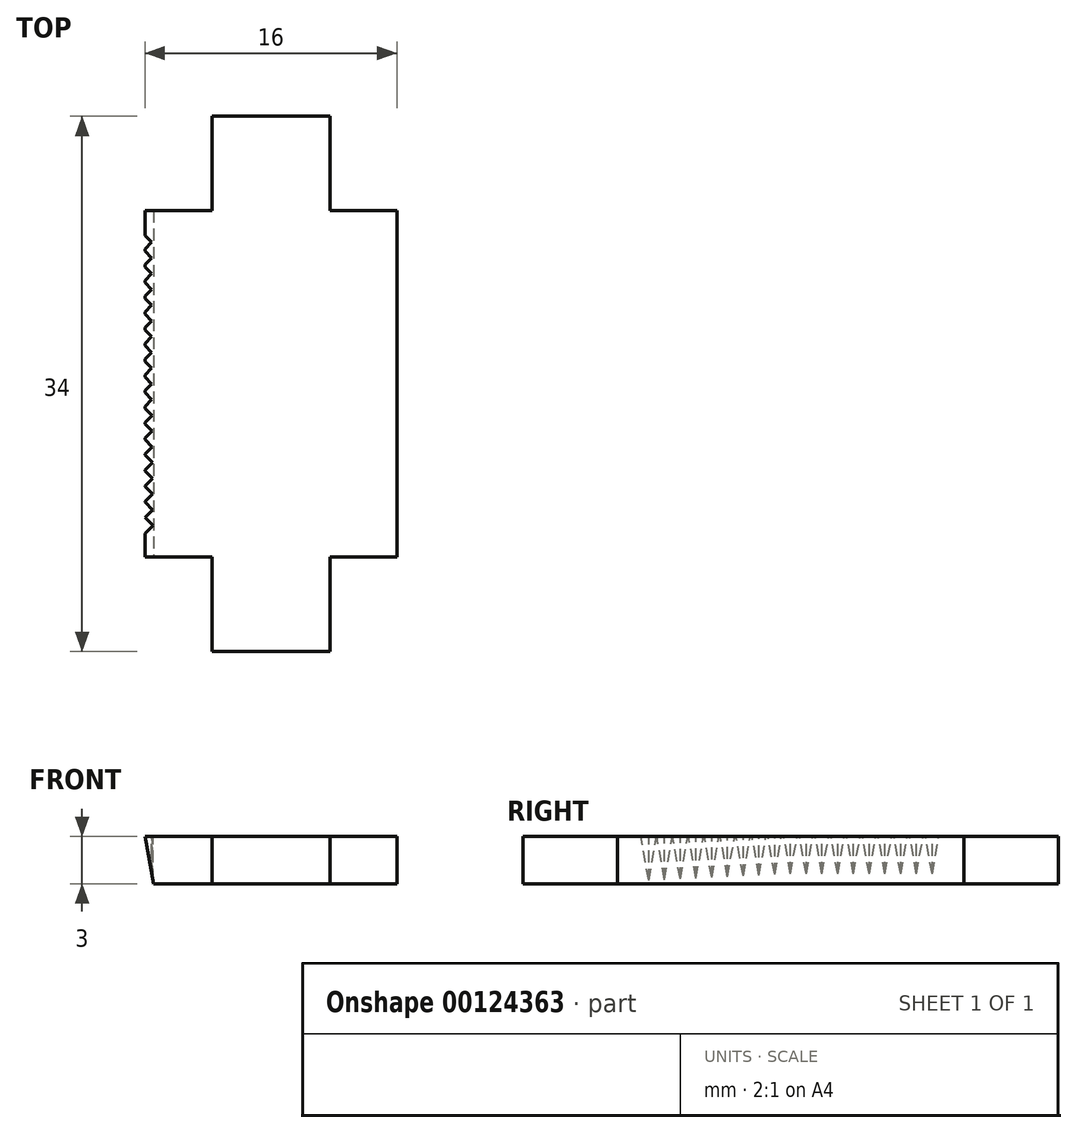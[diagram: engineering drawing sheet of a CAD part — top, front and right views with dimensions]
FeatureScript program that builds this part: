
annotation { "Feature Type Name" : "Feature", "Feature Type Description" : "" }
export const myFeature = defineFeature(function(context is Context, id is Id, definition is map)
    precondition{}
    {
        {
            var Q0;
            Q0=qCreatedBy(makeId("Front.planeOp"),FACE);
            var sketch = newSketch(context, id + "F0", { "sketchPlane" : qUnion([Q0])});
            skLineSegment(sketch, "E0.bottom", {"start": v(8, -1.5) * mm, "end": v(-8, -1.5) * mm});
            skLineSegment(sketch, "E0.top", {"start": v(8, 1.5) * mm, "end": v(-8, 1.5) * mm});
            skLineSegment(sketch, "E0.left", {"start": v(8, -1.5) * mm, "end": v(8, 1.5) * mm});
            skLineSegment(sketch, "E0.right", {"start": v(-8, -1.5) * mm, "end": v(-8, 1.5) * mm});
            skPoint(sketch, "E0.middle", {"position": v(0, 0) * mm});
            skSolve(sketch);
        }
        {
            var Q0;
            Q0=makeQuery(id+"F0.imprint","IMPRINT",FACE,{"disambiguationData":[TD([[makeQuery(id+"F0.imprint","IMPRINT",EDGE,{"derivedFrom":sQuery(id+"F0.wireOp",EDGE,"E0.bottom")}),-1.0]])]});
            extrude(context, id + "F1", {"entities" : qUnion([Q0]), "depth" : 22 * mm});
        }
        {
            var Q0;
            Q0=makeQuery(id+"F1.opExtrude","CAP_FACE",FACE,{"disambiguationData":[OSD([sQuery(id+"F0.wireOp",EDGE,"E0.bottom"),sQuery(id+"F0.wireOp",EDGE,"E0.top"),sQuery(id+"F0.wireOp",EDGE,"E0.left"),sQuery(id+"F0.wireOp",EDGE,"E0.right")])],"isStart":false});
            var sketch = newSketch(context, id + "F2", { "sketchPlane" : qUnion([Q0])});
            skLineSegment(sketch, "E1.bottom", {"start": v(3.75, -1.5) * mm, "end": v(-3.75, -1.5) * mm});
            skLineSegment(sketch, "E1.top", {"start": v(3.75, 1.5) * mm, "end": v(-3.75, 1.5) * mm});
            skLineSegment(sketch, "E1.left", {"start": v(3.75, -1.5) * mm, "end": v(3.75, 1.5) * mm});
            skLineSegment(sketch, "E1.right", {"start": v(-3.75, -1.5) * mm, "end": v(-3.75, 1.5) * mm});
            skPoint(sketch, "E1.middle", {"position": v(0, 0) * mm});
            skSolve(sketch);
        }
        {
            var Q0;
            Q0=makeQuery(id+"F2.imprint","IMPRINT",FACE,{"disambiguationData":[TD([[makeQuery(id+"F2.imprint","IMPRINT",EDGE,{"derivedFrom":sQuery(id+"F2.wireOp",EDGE,"E1.bottom")}),-1.0]])]});
            extrude(context, id + "F3", {"entities" : qUnion([Q0]), "operationType" : NewBodyOperationType.ADD, "depth" : 6 * mm});
        }
        {
            var Q0;
            Q0=makeQuery(id+"F1.opExtrude","CAP_FACE",FACE,{"disambiguationData":[OSD([sQuery(id+"F0.wireOp",EDGE,"E0.bottom"),sQuery(id+"F0.wireOp",EDGE,"E0.top"),sQuery(id+"F0.wireOp",EDGE,"E0.left"),sQuery(id+"F0.wireOp",EDGE,"E0.right")])],"isStart":true});
            var sketch = newSketch(context, id + "F4", { "sketchPlane" : qUnion([Q0])});
            skLineSegment(sketch, "E2.bottom", {"start": v(-3.75, -1.5) * mm, "end": v(3.75, -1.5) * mm});
            skLineSegment(sketch, "E2.top", {"start": v(-3.75, 1.5) * mm, "end": v(3.75, 1.5) * mm});
            skLineSegment(sketch, "E2.left", {"start": v(-3.75, -1.5) * mm, "end": v(-3.75, 1.5) * mm});
            skLineSegment(sketch, "E2.right", {"start": v(3.75, -1.5) * mm, "end": v(3.75, 1.5) * mm});
            skPoint(sketch, "E2.middle", {"position": v(0, 0) * mm});
            skSolve(sketch);
        }
        {
            var Q0;
            Q0=makeQuery(id+"F4.imprint","IMPRINT",FACE,{"disambiguationData":[TD([[makeQuery(id+"F4.imprint","IMPRINT",EDGE,{"derivedFrom":sQuery(id+"F4.wireOp",EDGE,"E2.bottom")}),1.0]])]});
            extrude(context, id + "F5", {"entities" : qUnion([Q0]), "operationType" : NewBodyOperationType.ADD, "depth" : 6 * mm});
        }
        {
            var Q0;
            Q0=makeQuery(id+"F5.boolean.opBoolean","MERGE",FACE,{"derivedFrom":[makeQuery(id+"F3.boolean.opBoolean","MERGE",FACE,{"derivedFrom":[makeQuery(id+"F1.opExtrude","SWEPT_FACE",FACE,{"disambiguationData":[OSD([sQuery(id+"F0.wireOp",EDGE,"E0.top")])]}),makeQuery(id+"F3.opExtrude","SWEPT_FACE",FACE,{"disambiguationData":[OSD([sQuery(id+"F2.wireOp",EDGE,"E1.top")])]})]}),makeQuery(id+"F5.opExtrude","SWEPT_FACE",FACE,{"disambiguationData":[OSD([sQuery(id+"F4.wireOp",EDGE,"E2.top")])]})]});
            var sketch = newSketch(context, id + "F6", { "sketchPlane" : qUnion([Q0])});
            skLineSegment(sketch, "E3", {"start": v(-8, -11) * mm, "end": v(8, -11) * mm, "construction": true});
            skLineSegment(sketch, "E4", {"start": v(-7.5, -11) * mm, "end": v(-8, -10.5) * mm});
            skLineSegment(sketch, "E5", {"start": v(-7.5, -11) * mm, "end": v(-8, -11.5) * mm});
            skPoint(sketch, "E6.orphan", {"position": v(-8.5, -10) * mm});
            skPoint(sketch, "E7.0.1.0", {"position": v(-8.5, -11) * mm});
            skLineSegment(sketch, "E7.0.1.1", {"start": v(-7.5, -12) * mm, "end": v(-8, -12.5) * mm});
            skLineSegment(sketch, "E7.0.1.2", {"start": v(-7.5, -12) * mm, "end": v(-8, -11.5) * mm});
            skPoint(sketch, "E7.0.2.0", {"position": v(-8.5, -12) * mm});
            skLineSegment(sketch, "E7.0.2.1", {"start": v(-7.5, -13) * mm, "end": v(-8, -13.5) * mm});
            skLineSegment(sketch, "E7.0.2.2", {"start": v(-7.5, -13) * mm, "end": v(-8, -12.5) * mm});
            skPoint(sketch, "E7.0.3.0", {"position": v(-8.5, -13) * mm});
            skLineSegment(sketch, "E7.0.3.1", {"start": v(-7.5, -14) * mm, "end": v(-8, -14.5) * mm});
            skLineSegment(sketch, "E7.0.3.2", {"start": v(-7.5, -14) * mm, "end": v(-8, -13.5) * mm});
            skPoint(sketch, "E7.0.4.0", {"position": v(-8.5, -14) * mm});
            skLineSegment(sketch, "E7.0.4.1", {"start": v(-7.5, -15) * mm, "end": v(-8, -15.5) * mm});
            skLineSegment(sketch, "E7.0.4.2", {"start": v(-7.5, -15) * mm, "end": v(-8, -14.5) * mm});
            skPoint(sketch, "E7.0.5.0", {"position": v(-8.5, -15) * mm});
            skLineSegment(sketch, "E7.0.5.1", {"start": v(-7.5, -16) * mm, "end": v(-8, -16.5) * mm});
            skLineSegment(sketch, "E7.0.5.2", {"start": v(-7.5, -16) * mm, "end": v(-8, -15.5) * mm});
            skPoint(sketch, "E7.0.6.0", {"position": v(-8.5, -16) * mm});
            skLineSegment(sketch, "E7.0.6.1", {"start": v(-7.5, -17) * mm, "end": v(-8, -17.5) * mm});
            skLineSegment(sketch, "E7.0.6.2", {"start": v(-7.5, -17) * mm, "end": v(-8, -16.5) * mm});
            skPoint(sketch, "E7.0.7.0", {"position": v(-8.5, -17) * mm});
            skLineSegment(sketch, "E7.0.7.1", {"start": v(-7.5, -18) * mm, "end": v(-8, -18.5) * mm});
            skLineSegment(sketch, "E7.0.7.2", {"start": v(-7.5, -18) * mm, "end": v(-8, -17.5) * mm});
            skPoint(sketch, "E7.0.8.0", {"position": v(-8.5, -18) * mm});
            skLineSegment(sketch, "E7.0.8.1", {"start": v(-7.5, -19) * mm, "end": v(-8, -19.5) * mm});
            skLineSegment(sketch, "E7.0.8.2", {"start": v(-7.5, -19) * mm, "end": v(-8, -18.5) * mm});
            skPoint(sketch, "E7.0.9.0", {"position": v(-8.5, -19) * mm});
            skLineSegment(sketch, "E7.0.9.1", {"start": v(-7.5, -20) * mm, "end": v(-8, -20.5) * mm});
            skLineSegment(sketch, "E7.0.9.2", {"start": v(-7.5, -20) * mm, "end": v(-8, -19.5) * mm});
            skPoint(sketch, "E7.1.0.0", {"position": v(-8.5, -9) * mm});
            skLineSegment(sketch, "E7.1.0.1", {"start": v(-7.5, -10) * mm, "end": v(-8, -10.5) * mm});
            skLineSegment(sketch, "E7.1.0.2", {"start": v(-7.5, -10) * mm, "end": v(-8, -9.5) * mm});
            skPoint(sketch, "E7.1.2.0", {"position": v(-8.5, -11) * mm});
            skLineSegment(sketch, "E7.1.2.1", {"start": v(-7.5, -12) * mm, "end": v(-8, -12.5) * mm});
            skLineSegment(sketch, "E7.1.2.2", {"start": v(-7.5, -12) * mm, "end": v(-8, -11.5) * mm});
            skPoint(sketch, "E7.1.3.0", {"position": v(-8.5, -12) * mm});
            skLineSegment(sketch, "E7.1.3.1", {"start": v(-7.5, -13) * mm, "end": v(-8, -13.5) * mm});
            skLineSegment(sketch, "E7.1.3.2", {"start": v(-7.5, -13) * mm, "end": v(-8, -12.5) * mm});
            skPoint(sketch, "E7.1.4.0", {"position": v(-8.5, -13) * mm});
            skLineSegment(sketch, "E7.1.4.1", {"start": v(-7.5, -14) * mm, "end": v(-8, -14.5) * mm});
            skLineSegment(sketch, "E7.1.4.2", {"start": v(-7.5, -14) * mm, "end": v(-8, -13.5) * mm});
            skPoint(sketch, "E7.1.5.0", {"position": v(-8.5, -14) * mm});
            skLineSegment(sketch, "E7.1.5.1", {"start": v(-7.5, -15) * mm, "end": v(-8, -15.5) * mm});
            skLineSegment(sketch, "E7.1.5.2", {"start": v(-7.5, -15) * mm, "end": v(-8, -14.5) * mm});
            skPoint(sketch, "E7.1.6.0", {"position": v(-8.5, -15) * mm});
            skLineSegment(sketch, "E7.1.6.1", {"start": v(-7.5, -16) * mm, "end": v(-8, -16.5) * mm});
            skLineSegment(sketch, "E7.1.6.2", {"start": v(-7.5, -16) * mm, "end": v(-8, -15.5) * mm});
            skPoint(sketch, "E7.1.7.0", {"position": v(-8.5, -16) * mm});
            skLineSegment(sketch, "E7.1.7.1", {"start": v(-7.5, -17) * mm, "end": v(-8, -17.5) * mm});
            skLineSegment(sketch, "E7.1.7.2", {"start": v(-7.5, -17) * mm, "end": v(-8, -16.5) * mm});
            skPoint(sketch, "E7.1.8.0", {"position": v(-8.5, -17) * mm});
            skLineSegment(sketch, "E7.1.8.1", {"start": v(-7.5, -18) * mm, "end": v(-8, -18.5) * mm});
            skLineSegment(sketch, "E7.1.8.2", {"start": v(-7.5, -18) * mm, "end": v(-8, -17.5) * mm});
            skPoint(sketch, "E7.1.9.0", {"position": v(-8.5, -18) * mm});
            skLineSegment(sketch, "E7.1.9.1", {"start": v(-7.5, -19) * mm, "end": v(-8, -19.5) * mm});
            skLineSegment(sketch, "E7.1.9.2", {"start": v(-7.5, -19) * mm, "end": v(-8, -18.5) * mm});
            skPoint(sketch, "E7.2.0.0", {"position": v(-8.52, -8) * mm});
            skLineSegment(sketch, "E7.2.0.1", {"start": v(-7.52, -9) * mm, "end": v(-8.02, -9.5) * mm});
            skLineSegment(sketch, "E7.2.0.2", {"start": v(-7.52, -9) * mm, "end": v(-8.02, -8.5) * mm});
            skPoint(sketch, "E7.2.1.0", {"position": v(-8.52, -9) * mm});
            skLineSegment(sketch, "E7.2.1.1", {"start": v(-7.52, -10) * mm, "end": v(-8.02, -10.5) * mm});
            skLineSegment(sketch, "E7.2.1.2", {"start": v(-7.52, -10) * mm, "end": v(-8.02, -9.5) * mm});
            skPoint(sketch, "E7.2.2.0", {"position": v(-8.52, -10) * mm});
            skLineSegment(sketch, "E7.2.2.1", {"start": v(-7.52, -11) * mm, "end": v(-8.02, -11.5) * mm});
            skLineSegment(sketch, "E7.2.2.2", {"start": v(-7.52, -11) * mm, "end": v(-8.02, -10.5) * mm});
            skPoint(sketch, "E7.2.3.0", {"position": v(-8.52, -11) * mm});
            skLineSegment(sketch, "E7.2.3.1", {"start": v(-7.52, -12) * mm, "end": v(-8.02, -12.5) * mm});
            skLineSegment(sketch, "E7.2.3.2", {"start": v(-7.52, -12) * mm, "end": v(-8.02, -11.5) * mm});
            skPoint(sketch, "E7.2.4.0", {"position": v(-8.52, -12) * mm});
            skLineSegment(sketch, "E7.2.4.1", {"start": v(-7.52, -13) * mm, "end": v(-8.02, -13.5) * mm});
            skLineSegment(sketch, "E7.2.4.2", {"start": v(-7.52, -13) * mm, "end": v(-8.02, -12.5) * mm});
            skPoint(sketch, "E7.2.5.0", {"position": v(-8.52, -13) * mm});
            skLineSegment(sketch, "E7.2.5.1", {"start": v(-7.52, -14) * mm, "end": v(-8.02, -14.5) * mm});
            skLineSegment(sketch, "E7.2.5.2", {"start": v(-7.52, -14) * mm, "end": v(-8.02, -13.5) * mm});
            skPoint(sketch, "E7.2.6.0", {"position": v(-8.52, -14) * mm});
            skLineSegment(sketch, "E7.2.6.1", {"start": v(-7.52, -15) * mm, "end": v(-8.02, -15.5) * mm});
            skLineSegment(sketch, "E7.2.6.2", {"start": v(-7.52, -15) * mm, "end": v(-8.02, -14.5) * mm});
            skPoint(sketch, "E7.2.7.0", {"position": v(-8.52, -15) * mm});
            skLineSegment(sketch, "E7.2.7.1", {"start": v(-7.52, -16) * mm, "end": v(-8.02, -16.5) * mm});
            skLineSegment(sketch, "E7.2.7.2", {"start": v(-7.52, -16) * mm, "end": v(-8.02, -15.5) * mm});
            skPoint(sketch, "E7.2.8.0", {"position": v(-8.52, -16) * mm});
            skLineSegment(sketch, "E7.2.8.1", {"start": v(-7.52, -17) * mm, "end": v(-8.02, -17.5) * mm});
            skLineSegment(sketch, "E7.2.8.2", {"start": v(-7.52, -17) * mm, "end": v(-8.02, -16.5) * mm});
            skPoint(sketch, "E7.2.9.0", {"position": v(-8.52, -17) * mm});
            skLineSegment(sketch, "E7.2.9.1", {"start": v(-7.52, -18) * mm, "end": v(-8.02, -18.5) * mm});
            skLineSegment(sketch, "E7.2.9.2", {"start": v(-7.52, -18) * mm, "end": v(-8.02, -17.5) * mm});
            skPoint(sketch, "E7.3.0.0", {"position": v(-8.52, -7) * mm});
            skLineSegment(sketch, "E7.3.0.1", {"start": v(-7.52, -8) * mm, "end": v(-8.02, -8.5) * mm});
            skLineSegment(sketch, "E7.3.0.2", {"start": v(-7.52, -8) * mm, "end": v(-8.02, -7.5) * mm});
            skPoint(sketch, "E7.3.1.0", {"position": v(-8.52, -8) * mm});
            skLineSegment(sketch, "E7.3.1.1", {"start": v(-7.52, -9) * mm, "end": v(-8.02, -9.5) * mm});
            skLineSegment(sketch, "E7.3.1.2", {"start": v(-7.52, -9) * mm, "end": v(-8.02, -8.5) * mm});
            skPoint(sketch, "E7.3.2.0", {"position": v(-8.52, -9) * mm});
            skLineSegment(sketch, "E7.3.2.1", {"start": v(-7.52, -10) * mm, "end": v(-8.02, -10.5) * mm});
            skLineSegment(sketch, "E7.3.2.2", {"start": v(-7.52, -10) * mm, "end": v(-8.02, -9.5) * mm});
            skPoint(sketch, "E7.3.3.0", {"position": v(-8.52, -10) * mm});
            skLineSegment(sketch, "E7.3.3.1", {"start": v(-7.52, -11) * mm, "end": v(-8.02, -11.5) * mm});
            skLineSegment(sketch, "E7.3.3.2", {"start": v(-7.52, -11) * mm, "end": v(-8.02, -10.5) * mm});
            skPoint(sketch, "E7.3.4.0", {"position": v(-8.52, -11) * mm});
            skLineSegment(sketch, "E7.3.4.1", {"start": v(-7.52, -12) * mm, "end": v(-8.02, -12.5) * mm});
            skLineSegment(sketch, "E7.3.4.2", {"start": v(-7.52, -12) * mm, "end": v(-8.02, -11.5) * mm});
            skPoint(sketch, "E7.3.5.0", {"position": v(-8.52, -12) * mm});
            skLineSegment(sketch, "E7.3.5.1", {"start": v(-7.52, -13) * mm, "end": v(-8.02, -13.5) * mm});
            skLineSegment(sketch, "E7.3.5.2", {"start": v(-7.52, -13) * mm, "end": v(-8.02, -12.5) * mm});
            skPoint(sketch, "E7.3.6.0", {"position": v(-8.52, -13) * mm});
            skLineSegment(sketch, "E7.3.6.1", {"start": v(-7.52, -14) * mm, "end": v(-8.02, -14.5) * mm});
            skLineSegment(sketch, "E7.3.6.2", {"start": v(-7.52, -14) * mm, "end": v(-8.02, -13.5) * mm});
            skPoint(sketch, "E7.3.7.0", {"position": v(-8.52, -14) * mm});
            skLineSegment(sketch, "E7.3.7.1", {"start": v(-7.52, -15) * mm, "end": v(-8.02, -15.5) * mm});
            skLineSegment(sketch, "E7.3.7.2", {"start": v(-7.52, -15) * mm, "end": v(-8.02, -14.5) * mm});
            skPoint(sketch, "E7.3.8.0", {"position": v(-8.52, -15) * mm});
            skLineSegment(sketch, "E7.3.8.1", {"start": v(-7.52, -16) * mm, "end": v(-8.02, -16.5) * mm});
            skLineSegment(sketch, "E7.3.8.2", {"start": v(-7.52, -16) * mm, "end": v(-8.02, -15.5) * mm});
            skPoint(sketch, "E7.3.9.0", {"position": v(-8.52, -16) * mm});
            skLineSegment(sketch, "E7.3.9.1", {"start": v(-7.52, -17) * mm, "end": v(-8.02, -17.5) * mm});
            skLineSegment(sketch, "E7.3.9.2", {"start": v(-7.52, -17) * mm, "end": v(-8.02, -16.5) * mm});
            skPoint(sketch, "E7.4.0.0", {"position": v(-8.53, -6) * mm});
            skLineSegment(sketch, "E7.4.0.1", {"start": v(-7.53, -7) * mm, "end": v(-8.03, -7.5) * mm});
            skLineSegment(sketch, "E7.4.0.2", {"start": v(-7.53, -7) * mm, "end": v(-8.03, -6.5) * mm});
            skPoint(sketch, "E7.4.1.0", {"position": v(-8.53, -7) * mm});
            skLineSegment(sketch, "E7.4.1.1", {"start": v(-7.53, -8) * mm, "end": v(-8.03, -8.5) * mm});
            skLineSegment(sketch, "E7.4.1.2", {"start": v(-7.53, -8) * mm, "end": v(-8.03, -7.5) * mm});
            skPoint(sketch, "E7.4.2.0", {"position": v(-8.53, -8) * mm});
            skLineSegment(sketch, "E7.4.2.1", {"start": v(-7.53, -9) * mm, "end": v(-8.03, -9.5) * mm});
            skLineSegment(sketch, "E7.4.2.2", {"start": v(-7.53, -9) * mm, "end": v(-8.03, -8.5) * mm});
            skPoint(sketch, "E7.4.3.0", {"position": v(-8.53, -9) * mm});
            skLineSegment(sketch, "E7.4.3.1", {"start": v(-7.53, -10) * mm, "end": v(-8.03, -10.5) * mm});
            skLineSegment(sketch, "E7.4.3.2", {"start": v(-7.53, -10) * mm, "end": v(-8.03, -9.5) * mm});
            skPoint(sketch, "E7.4.4.0", {"position": v(-8.53, -10) * mm});
            skLineSegment(sketch, "E7.4.4.1", {"start": v(-7.53, -11) * mm, "end": v(-8.03, -11.5) * mm});
            skLineSegment(sketch, "E7.4.4.2", {"start": v(-7.53, -11) * mm, "end": v(-8.03, -10.5) * mm});
            skPoint(sketch, "E7.4.5.0", {"position": v(-8.53, -11) * mm});
            skLineSegment(sketch, "E7.4.5.1", {"start": v(-7.53, -12) * mm, "end": v(-8.03, -12.5) * mm});
            skLineSegment(sketch, "E7.4.5.2", {"start": v(-7.53, -12) * mm, "end": v(-8.03, -11.5) * mm});
            skPoint(sketch, "E7.4.6.0", {"position": v(-8.53, -12) * mm});
            skLineSegment(sketch, "E7.4.6.1", {"start": v(-7.53, -13) * mm, "end": v(-8.03, -13.5) * mm});
            skLineSegment(sketch, "E7.4.6.2", {"start": v(-7.53, -13) * mm, "end": v(-8.03, -12.5) * mm});
            skPoint(sketch, "E7.4.7.0", {"position": v(-8.53, -13) * mm});
            skLineSegment(sketch, "E7.4.7.1", {"start": v(-7.53, -14) * mm, "end": v(-8.03, -14.5) * mm});
            skLineSegment(sketch, "E7.4.7.2", {"start": v(-7.53, -14) * mm, "end": v(-8.03, -13.5) * mm});
            skPoint(sketch, "E7.4.8.0", {"position": v(-8.53, -14) * mm});
            skLineSegment(sketch, "E7.4.8.1", {"start": v(-7.53, -15) * mm, "end": v(-8.03, -15.5) * mm});
            skLineSegment(sketch, "E7.4.8.2", {"start": v(-7.53, -15) * mm, "end": v(-8.03, -14.5) * mm});
            skPoint(sketch, "E7.4.9.0", {"position": v(-8.53, -15) * mm});
            skLineSegment(sketch, "E7.4.9.1", {"start": v(-7.53, -16) * mm, "end": v(-8.03, -16.5) * mm});
            skLineSegment(sketch, "E7.4.9.2", {"start": v(-7.53, -16) * mm, "end": v(-8.03, -15.5) * mm});
            skPoint(sketch, "E7.5.0.0", {"position": v(-8.54, -5) * mm});
            skLineSegment(sketch, "E7.5.0.1", {"start": v(-7.54, -6) * mm, "end": v(-8.04, -6.5) * mm});
            skLineSegment(sketch, "E7.5.0.2", {"start": v(-7.54, -6) * mm, "end": v(-8.04, -5.5) * mm});
            skPoint(sketch, "E7.5.1.0", {"position": v(-8.54, -6) * mm});
            skLineSegment(sketch, "E7.5.1.1", {"start": v(-7.54, -7) * mm, "end": v(-8.04, -7.5) * mm});
            skLineSegment(sketch, "E7.5.1.2", {"start": v(-7.54, -7) * mm, "end": v(-8.04, -6.5) * mm});
            skPoint(sketch, "E7.5.2.0", {"position": v(-8.54, -7) * mm});
            skLineSegment(sketch, "E7.5.2.1", {"start": v(-7.54, -8) * mm, "end": v(-8.04, -8.5) * mm});
            skLineSegment(sketch, "E7.5.2.2", {"start": v(-7.54, -8) * mm, "end": v(-8.04, -7.5) * mm});
            skPoint(sketch, "E7.5.3.0", {"position": v(-8.54, -8) * mm});
            skLineSegment(sketch, "E7.5.3.1", {"start": v(-7.54, -9) * mm, "end": v(-8.04, -9.5) * mm});
            skLineSegment(sketch, "E7.5.3.2", {"start": v(-7.54, -9) * mm, "end": v(-8.04, -8.5) * mm});
            skPoint(sketch, "E7.5.4.0", {"position": v(-8.54, -9) * mm});
            skLineSegment(sketch, "E7.5.4.1", {"start": v(-7.54, -10) * mm, "end": v(-8.04, -10.5) * mm});
            skLineSegment(sketch, "E7.5.4.2", {"start": v(-7.54, -10) * mm, "end": v(-8.04, -9.5) * mm});
            skPoint(sketch, "E7.5.5.0", {"position": v(-8.54, -10) * mm});
            skLineSegment(sketch, "E7.5.5.1", {"start": v(-7.54, -11) * mm, "end": v(-8.04, -11.5) * mm});
            skLineSegment(sketch, "E7.5.5.2", {"start": v(-7.54, -11) * mm, "end": v(-8.04, -10.5) * mm});
            skPoint(sketch, "E7.5.6.0", {"position": v(-8.54, -11) * mm});
            skLineSegment(sketch, "E7.5.6.1", {"start": v(-7.54, -12) * mm, "end": v(-8.04, -12.5) * mm});
            skLineSegment(sketch, "E7.5.6.2", {"start": v(-7.54, -12) * mm, "end": v(-8.04, -11.5) * mm});
            skPoint(sketch, "E7.5.7.0", {"position": v(-8.54, -12) * mm});
            skLineSegment(sketch, "E7.5.7.1", {"start": v(-7.54, -13) * mm, "end": v(-8.04, -13.5) * mm});
            skLineSegment(sketch, "E7.5.7.2", {"start": v(-7.54, -13) * mm, "end": v(-8.04, -12.5) * mm});
            skPoint(sketch, "E7.5.8.0", {"position": v(-8.54, -13) * mm});
            skLineSegment(sketch, "E7.5.8.1", {"start": v(-7.54, -14) * mm, "end": v(-8.04, -14.5) * mm});
            skLineSegment(sketch, "E7.5.8.2", {"start": v(-7.54, -14) * mm, "end": v(-8.04, -13.5) * mm});
            skPoint(sketch, "E7.5.9.0", {"position": v(-8.54, -14) * mm});
            skLineSegment(sketch, "E7.5.9.1", {"start": v(-7.54, -15) * mm, "end": v(-8.04, -15.5) * mm});
            skLineSegment(sketch, "E7.5.9.2", {"start": v(-7.54, -15) * mm, "end": v(-8.04, -14.5) * mm});
            skPoint(sketch, "E7.6.0.0", {"position": v(-8.55, -4) * mm});
            skLineSegment(sketch, "E7.6.0.1", {"start": v(-7.55, -5) * mm, "end": v(-8.05, -5.5) * mm});
            skLineSegment(sketch, "E7.6.0.2", {"start": v(-7.55, -5) * mm, "end": v(-8.05, -4.5) * mm});
            skPoint(sketch, "E7.6.1.0", {"position": v(-8.55, -5) * mm});
            skLineSegment(sketch, "E7.6.1.1", {"start": v(-7.55, -6) * mm, "end": v(-8.05, -6.5) * mm});
            skLineSegment(sketch, "E7.6.1.2", {"start": v(-7.55, -6) * mm, "end": v(-8.05, -5.5) * mm});
            skPoint(sketch, "E7.6.2.0", {"position": v(-8.55, -6) * mm});
            skLineSegment(sketch, "E7.6.2.1", {"start": v(-7.55, -7) * mm, "end": v(-8.05, -7.5) * mm});
            skLineSegment(sketch, "E7.6.2.2", {"start": v(-7.55, -7) * mm, "end": v(-8.05, -6.5) * mm});
            skPoint(sketch, "E7.6.3.0", {"position": v(-8.55, -7) * mm});
            skLineSegment(sketch, "E7.6.3.1", {"start": v(-7.55, -8) * mm, "end": v(-8.05, -8.5) * mm});
            skLineSegment(sketch, "E7.6.3.2", {"start": v(-7.55, -8) * mm, "end": v(-8.05, -7.5) * mm});
            skPoint(sketch, "E7.6.4.0", {"position": v(-8.55, -8) * mm});
            skLineSegment(sketch, "E7.6.4.1", {"start": v(-7.55, -9) * mm, "end": v(-8.05, -9.5) * mm});
            skLineSegment(sketch, "E7.6.4.2", {"start": v(-7.55, -9) * mm, "end": v(-8.05, -8.5) * mm});
            skPoint(sketch, "E7.6.5.0", {"position": v(-8.55, -9) * mm});
            skLineSegment(sketch, "E7.6.5.1", {"start": v(-7.55, -10) * mm, "end": v(-8.05, -10.5) * mm});
            skLineSegment(sketch, "E7.6.5.2", {"start": v(-7.55, -10) * mm, "end": v(-8.05, -9.5) * mm});
            skPoint(sketch, "E7.6.6.0", {"position": v(-8.55, -10) * mm});
            skLineSegment(sketch, "E7.6.6.1", {"start": v(-7.55, -11) * mm, "end": v(-8.05, -11.5) * mm});
            skLineSegment(sketch, "E7.6.6.2", {"start": v(-7.55, -11) * mm, "end": v(-8.05, -10.5) * mm});
            skPoint(sketch, "E7.6.7.0", {"position": v(-8.55, -11) * mm});
            skLineSegment(sketch, "E7.6.7.1", {"start": v(-7.55, -12) * mm, "end": v(-8.05, -12.5) * mm});
            skLineSegment(sketch, "E7.6.7.2", {"start": v(-7.55, -12) * mm, "end": v(-8.05, -11.5) * mm});
            skPoint(sketch, "E7.6.8.0", {"position": v(-8.55, -12) * mm});
            skLineSegment(sketch, "E7.6.8.1", {"start": v(-7.55, -13) * mm, "end": v(-8.05, -13.5) * mm});
            skLineSegment(sketch, "E7.6.8.2", {"start": v(-7.55, -13) * mm, "end": v(-8.05, -12.5) * mm});
            skPoint(sketch, "E7.6.9.0", {"position": v(-8.55, -13) * mm});
            skLineSegment(sketch, "E7.6.9.1", {"start": v(-7.55, -14) * mm, "end": v(-8.05, -14.5) * mm});
            skLineSegment(sketch, "E7.6.9.2", {"start": v(-7.55, -14) * mm, "end": v(-8.05, -13.5) * mm});
            skPoint(sketch, "E7.7.0.0", {"position": v(-8.56, -3) * mm});
            skLineSegment(sketch, "E7.7.0.1", {"start": v(-7.56, -4) * mm, "end": v(-8.06, -4.5) * mm});
            skLineSegment(sketch, "E7.7.0.2", {"start": v(-7.56, -4) * mm, "end": v(-8.06, -3.5) * mm});
            skPoint(sketch, "E7.7.1.0", {"position": v(-8.56, -4) * mm});
            skLineSegment(sketch, "E7.7.1.1", {"start": v(-7.56, -5) * mm, "end": v(-8.06, -5.5) * mm});
            skLineSegment(sketch, "E7.7.1.2", {"start": v(-7.56, -5) * mm, "end": v(-8.06, -4.5) * mm});
            skPoint(sketch, "E7.7.2.0", {"position": v(-8.56, -5) * mm});
            skLineSegment(sketch, "E7.7.2.1", {"start": v(-7.56, -6) * mm, "end": v(-8.06, -6.5) * mm});
            skLineSegment(sketch, "E7.7.2.2", {"start": v(-7.56, -6) * mm, "end": v(-8.06, -5.5) * mm});
            skPoint(sketch, "E7.7.3.0", {"position": v(-8.56, -6) * mm});
            skLineSegment(sketch, "E7.7.3.1", {"start": v(-7.56, -7) * mm, "end": v(-8.06, -7.5) * mm});
            skLineSegment(sketch, "E7.7.3.2", {"start": v(-7.56, -7) * mm, "end": v(-8.06, -6.5) * mm});
            skPoint(sketch, "E7.7.4.0", {"position": v(-8.56, -7) * mm});
            skLineSegment(sketch, "E7.7.4.1", {"start": v(-7.56, -8) * mm, "end": v(-8.06, -8.5) * mm});
            skLineSegment(sketch, "E7.7.4.2", {"start": v(-7.56, -8) * mm, "end": v(-8.06, -7.5) * mm});
            skPoint(sketch, "E7.7.5.0", {"position": v(-8.56, -8) * mm});
            skLineSegment(sketch, "E7.7.5.1", {"start": v(-7.56, -9) * mm, "end": v(-8.06, -9.5) * mm});
            skLineSegment(sketch, "E7.7.5.2", {"start": v(-7.56, -9) * mm, "end": v(-8.06, -8.5) * mm});
            skPoint(sketch, "E7.7.6.0", {"position": v(-8.56, -9) * mm});
            skLineSegment(sketch, "E7.7.6.1", {"start": v(-7.56, -10) * mm, "end": v(-8.06, -10.5) * mm});
            skLineSegment(sketch, "E7.7.6.2", {"start": v(-7.56, -10) * mm, "end": v(-8.06, -9.5) * mm});
            skPoint(sketch, "E7.7.7.0", {"position": v(-8.56, -10) * mm});
            skLineSegment(sketch, "E7.7.7.1", {"start": v(-7.56, -11) * mm, "end": v(-8.06, -11.5) * mm});
            skLineSegment(sketch, "E7.7.7.2", {"start": v(-7.56, -11) * mm, "end": v(-8.06, -10.5) * mm});
            skPoint(sketch, "E7.7.8.0", {"position": v(-8.56, -11) * mm});
            skLineSegment(sketch, "E7.7.8.1", {"start": v(-7.56, -12) * mm, "end": v(-8.06, -12.5) * mm});
            skLineSegment(sketch, "E7.7.8.2", {"start": v(-7.56, -12) * mm, "end": v(-8.06, -11.5) * mm});
            skPoint(sketch, "E7.7.9.0", {"position": v(-8.56, -12) * mm});
            skLineSegment(sketch, "E7.7.9.1", {"start": v(-7.56, -13) * mm, "end": v(-8.06, -13.5) * mm});
            skLineSegment(sketch, "E7.7.9.2", {"start": v(-7.56, -13) * mm, "end": v(-8.06, -12.5) * mm});
            skPoint(sketch, "E7.8.0.0", {"position": v(-8.57, -2) * mm});
            skLineSegment(sketch, "E7.8.0.1", {"start": v(-7.57, -3) * mm, "end": v(-8.07, -3.5) * mm});
            skLineSegment(sketch, "E7.8.0.2", {"start": v(-7.57, -3) * mm, "end": v(-8.07, -2.5) * mm});
            skPoint(sketch, "E7.8.1.0", {"position": v(-8.57, -3) * mm});
            skLineSegment(sketch, "E7.8.1.1", {"start": v(-7.57, -4) * mm, "end": v(-8.07, -4.5) * mm});
            skLineSegment(sketch, "E7.8.1.2", {"start": v(-7.57, -4) * mm, "end": v(-8.07, -3.5) * mm});
            skPoint(sketch, "E7.8.2.0", {"position": v(-8.57, -4) * mm});
            skLineSegment(sketch, "E7.8.2.1", {"start": v(-7.57, -5) * mm, "end": v(-8.07, -5.5) * mm});
            skLineSegment(sketch, "E7.8.2.2", {"start": v(-7.57, -5) * mm, "end": v(-8.07, -4.5) * mm});
            skPoint(sketch, "E7.8.3.0", {"position": v(-8.57, -5) * mm});
            skLineSegment(sketch, "E7.8.3.1", {"start": v(-7.57, -6) * mm, "end": v(-8.07, -6.5) * mm});
            skLineSegment(sketch, "E7.8.3.2", {"start": v(-7.57, -6) * mm, "end": v(-8.07, -5.5) * mm});
            skPoint(sketch, "E7.8.4.0", {"position": v(-8.57, -6) * mm});
            skLineSegment(sketch, "E7.8.4.1", {"start": v(-7.57, -7) * mm, "end": v(-8.07, -7.5) * mm});
            skLineSegment(sketch, "E7.8.4.2", {"start": v(-7.57, -7) * mm, "end": v(-8.07, -6.5) * mm});
            skPoint(sketch, "E7.8.5.0", {"position": v(-8.57, -7) * mm});
            skLineSegment(sketch, "E7.8.5.1", {"start": v(-7.57, -8) * mm, "end": v(-8.07, -8.5) * mm});
            skLineSegment(sketch, "E7.8.5.2", {"start": v(-7.57, -8) * mm, "end": v(-8.07, -7.5) * mm});
            skPoint(sketch, "E7.8.6.0", {"position": v(-8.57, -8) * mm});
            skLineSegment(sketch, "E7.8.6.1", {"start": v(-7.57, -9) * mm, "end": v(-8.07, -9.5) * mm});
            skLineSegment(sketch, "E7.8.6.2", {"start": v(-7.57, -9) * mm, "end": v(-8.07, -8.5) * mm});
            skPoint(sketch, "E7.8.7.0", {"position": v(-8.57, -9) * mm});
            skLineSegment(sketch, "E7.8.7.1", {"start": v(-7.57, -10) * mm, "end": v(-8.07, -10.5) * mm});
            skLineSegment(sketch, "E7.8.7.2", {"start": v(-7.57, -10) * mm, "end": v(-8.07, -9.5) * mm});
            skPoint(sketch, "E7.8.8.0", {"position": v(-8.57, -10) * mm});
            skLineSegment(sketch, "E7.8.8.1", {"start": v(-7.57, -11) * mm, "end": v(-8.07, -11.5) * mm});
            skLineSegment(sketch, "E7.8.8.2", {"start": v(-7.57, -11) * mm, "end": v(-8.07, -10.5) * mm});
            skPoint(sketch, "E7.8.9.0", {"position": v(-8.57, -11) * mm});
            skLineSegment(sketch, "E7.8.9.1", {"start": v(-7.57, -12) * mm, "end": v(-8.07, -12.5) * mm});
            skLineSegment(sketch, "E7.8.9.2", {"start": v(-7.57, -12) * mm, "end": v(-8.07, -11.5) * mm});
            skPoint(sketch, "E7.9.0.0", {"position": v(-8.57, -1) * mm});
            skLineSegment(sketch, "E7.9.0.1", {"start": v(-7.57, -2) * mm, "end": v(-8.07, -2.5) * mm});
            skLineSegment(sketch, "E7.9.0.2", {"start": v(-7.57, -2) * mm, "end": v(-8.07, -1.5) * mm});
            skPoint(sketch, "E7.9.1.0", {"position": v(-8.57, -2) * mm});
            skLineSegment(sketch, "E7.9.1.1", {"start": v(-7.57, -3) * mm, "end": v(-8.07, -3.5) * mm});
            skLineSegment(sketch, "E7.9.1.2", {"start": v(-7.57, -3) * mm, "end": v(-8.07, -2.5) * mm});
            skPoint(sketch, "E7.9.2.0", {"position": v(-8.57, -3) * mm});
            skLineSegment(sketch, "E7.9.2.1", {"start": v(-7.57, -4) * mm, "end": v(-8.07, -4.5) * mm});
            skLineSegment(sketch, "E7.9.2.2", {"start": v(-7.57, -4) * mm, "end": v(-8.07, -3.5) * mm});
            skPoint(sketch, "E7.9.3.0", {"position": v(-8.57, -4) * mm});
            skLineSegment(sketch, "E7.9.3.1", {"start": v(-7.57, -5) * mm, "end": v(-8.07, -5.5) * mm});
            skLineSegment(sketch, "E7.9.3.2", {"start": v(-7.57, -5) * mm, "end": v(-8.07, -4.5) * mm});
            skPoint(sketch, "E7.9.4.0", {"position": v(-8.57, -5) * mm});
            skLineSegment(sketch, "E7.9.4.1", {"start": v(-7.57, -6) * mm, "end": v(-8.07, -6.5) * mm});
            skLineSegment(sketch, "E7.9.4.2", {"start": v(-7.57, -6) * mm, "end": v(-8.07, -5.5) * mm});
            skPoint(sketch, "E7.9.5.0", {"position": v(-8.57, -6) * mm});
            skLineSegment(sketch, "E7.9.5.1", {"start": v(-7.57, -7) * mm, "end": v(-8.07, -7.5) * mm});
            skLineSegment(sketch, "E7.9.5.2", {"start": v(-7.57, -7) * mm, "end": v(-8.07, -6.5) * mm});
            skPoint(sketch, "E7.9.6.0", {"position": v(-8.57, -7) * mm});
            skLineSegment(sketch, "E7.9.6.1", {"start": v(-7.57, -8) * mm, "end": v(-8.07, -8.5) * mm});
            skLineSegment(sketch, "E7.9.6.2", {"start": v(-7.57, -8) * mm, "end": v(-8.07, -7.5) * mm});
            skPoint(sketch, "E7.9.7.0", {"position": v(-8.57, -8) * mm});
            skLineSegment(sketch, "E7.9.7.1", {"start": v(-7.57, -9) * mm, "end": v(-8.07, -9.5) * mm});
            skLineSegment(sketch, "E7.9.7.2", {"start": v(-7.57, -9) * mm, "end": v(-8.07, -8.5) * mm});
            skPoint(sketch, "E7.9.8.0", {"position": v(-8.57, -9) * mm});
            skLineSegment(sketch, "E7.9.8.1", {"start": v(-7.57, -10) * mm, "end": v(-8.07, -10.5) * mm});
            skLineSegment(sketch, "E7.9.8.2", {"start": v(-7.57, -10) * mm, "end": v(-8.07, -9.5) * mm});
            skPoint(sketch, "E7.9.9.0", {"position": v(-8.57, -10) * mm});
            skLineSegment(sketch, "E7.9.9.1", {"start": v(-7.57, -11) * mm, "end": v(-8.07, -11.5) * mm});
            skLineSegment(sketch, "E7.9.9.2", {"start": v(-7.57, -11) * mm, "end": v(-8.07, -10.5) * mm});
            skLineSegment(sketch, "E7.direction1", {"start": v(-8, -11.5) * mm, "end": v(-8, -10.5) * mm, "construction": true});
            skLineSegment(sketch, "E7.direction2", {"start": v(-8, -11.5) * mm, "end": v(-8, -12.5) * mm, "construction": true});
            skSolve(sketch);
        }
        {
            var Q0;
            Q0 = qSketchRegion(id + "F6", true);
            var Q1;
            {var subQ0=sQuery(id+"F6.wireOp",EDGE,"E7.9.0.2");var subQ1=sQuery(id+"F6.wireOp",EDGE,"E7.9.0.1");var subQ2=makeQuery(id+"F6.imprint","INTERSECT",VERTEX,{"derivedFrom":[subQ1,subQ0]});Q1=makeQuery(id+"F6.imprint","IMPRINT",FACE,{"disambiguationData":[TD([[makeQuery(id+"F6.imprint","IMPRINT",EDGE,{"disambiguationData":[TD([[subQ2,-1.0]])],"derivedFrom":subQ1}),-1.0]])]});}
            var Q2;
            {var subQ0=sQuery(id+"F6.wireOp",EDGE,"E7.9.1.2");var subQ1=sQuery(id+"F6.wireOp",EDGE,"E7.9.1.1");var subQ2=makeQuery(id+"F6.imprint","INTERSECT",VERTEX,{"derivedFrom":[subQ1,subQ0]});Q2=makeQuery(id+"F6.imprint","IMPRINT",FACE,{"disambiguationData":[TD([[makeQuery(id+"F6.imprint","IMPRINT",EDGE,{"disambiguationData":[TD([[subQ2,-1.0]])],"derivedFrom":subQ1}),-1.0]])]});}
            var Q3;
            {var subQ0=sQuery(id+"F6.wireOp",EDGE,"E7.9.2.2");var subQ1=sQuery(id+"F6.wireOp",EDGE,"E7.9.2.1");var subQ2=makeQuery(id+"F6.imprint","INTERSECT",VERTEX,{"derivedFrom":[subQ1,subQ0]});Q3=makeQuery(id+"F6.imprint","IMPRINT",FACE,{"disambiguationData":[TD([[makeQuery(id+"F6.imprint","IMPRINT",EDGE,{"disambiguationData":[TD([[subQ2,-1.0]])],"derivedFrom":subQ1}),-1.0]])]});}
            var Q4;
            {var subQ0=sQuery(id+"F6.wireOp",EDGE,"E7.9.3.2");var subQ1=sQuery(id+"F6.wireOp",EDGE,"E7.9.3.1");var subQ2=makeQuery(id+"F6.imprint","INTERSECT",VERTEX,{"derivedFrom":[subQ1,subQ0]});Q4=makeQuery(id+"F6.imprint","IMPRINT",FACE,{"disambiguationData":[TD([[makeQuery(id+"F6.imprint","IMPRINT",EDGE,{"disambiguationData":[TD([[subQ2,-1.0]])],"derivedFrom":subQ1}),-1.0]])]});}
            var Q5;
            {var subQ0=sQuery(id+"F6.wireOp",EDGE,"E7.9.4.2");var subQ1=sQuery(id+"F6.wireOp",EDGE,"E7.9.4.1");var subQ2=makeQuery(id+"F6.imprint","INTERSECT",VERTEX,{"derivedFrom":[subQ1,subQ0]});Q5=makeQuery(id+"F6.imprint","IMPRINT",FACE,{"disambiguationData":[TD([[makeQuery(id+"F6.imprint","IMPRINT",EDGE,{"disambiguationData":[TD([[subQ2,-1.0]])],"derivedFrom":subQ1}),-1.0]])]});}
            var Q6;
            {var subQ0=sQuery(id+"F6.wireOp",EDGE,"E7.9.5.2");var subQ1=sQuery(id+"F6.wireOp",EDGE,"E7.9.5.1");var subQ2=makeQuery(id+"F6.imprint","INTERSECT",VERTEX,{"derivedFrom":[subQ1,subQ0]});Q6=makeQuery(id+"F6.imprint","IMPRINT",FACE,{"disambiguationData":[TD([[makeQuery(id+"F6.imprint","IMPRINT",EDGE,{"disambiguationData":[TD([[subQ2,-1.0]])],"derivedFrom":subQ1}),-1.0]])]});}
            var Q7;
            {var subQ0=sQuery(id+"F6.wireOp",EDGE,"E7.9.6.2");var subQ1=sQuery(id+"F6.wireOp",EDGE,"E7.9.6.1");var subQ2=makeQuery(id+"F6.imprint","INTERSECT",VERTEX,{"derivedFrom":[subQ1,subQ0]});Q7=makeQuery(id+"F6.imprint","IMPRINT",FACE,{"disambiguationData":[TD([[makeQuery(id+"F6.imprint","IMPRINT",EDGE,{"disambiguationData":[TD([[subQ2,-1.0]])],"derivedFrom":subQ1}),-1.0]])]});}
            var Q8;
            {var subQ0=sQuery(id+"F6.wireOp",EDGE,"E7.9.7.2");var subQ1=sQuery(id+"F6.wireOp",EDGE,"E7.9.7.1");var subQ2=makeQuery(id+"F6.imprint","INTERSECT",VERTEX,{"derivedFrom":[subQ1,subQ0]});Q8=makeQuery(id+"F6.imprint","IMPRINT",FACE,{"disambiguationData":[TD([[makeQuery(id+"F6.imprint","IMPRINT",EDGE,{"disambiguationData":[TD([[subQ2,-1.0]])],"derivedFrom":subQ1}),-1.0]])]});}
            var Q9;
            {var subQ0=sQuery(id+"F6.wireOp",EDGE,"E7.9.8.2");var subQ1=sQuery(id+"F6.wireOp",EDGE,"E7.9.8.1");var subQ2=makeQuery(id+"F6.imprint","INTERSECT",VERTEX,{"derivedFrom":[subQ1,subQ0]});Q9=makeQuery(id+"F6.imprint","IMPRINT",FACE,{"disambiguationData":[TD([[makeQuery(id+"F6.imprint","IMPRINT",EDGE,{"disambiguationData":[TD([[subQ2,-1.0]])],"derivedFrom":subQ1}),-1.0]])]});}
            var Q10;
            {var subQ0=sQuery(id+"F6.wireOp",EDGE,"E7.9.9.2");var subQ1=sQuery(id+"F6.wireOp",EDGE,"E7.9.9.1");var subQ2=makeQuery(id+"F6.imprint","INTERSECT",VERTEX,{"derivedFrom":[subQ1,subQ0]});Q10=makeQuery(id+"F6.imprint","IMPRINT",FACE,{"disambiguationData":[TD([[makeQuery(id+"F6.imprint","IMPRINT",EDGE,{"disambiguationData":[TD([[subQ2,-1.0]])],"derivedFrom":subQ1}),-1.0]])]});}
            var Q11;
            {var subQ0=sQuery(id+"F6.wireOp",EDGE,"E7.8.9.2");var subQ1=sQuery(id+"F6.wireOp",EDGE,"E7.8.9.1");var subQ2=makeQuery(id+"F6.imprint","INTERSECT",VERTEX,{"derivedFrom":[subQ1,subQ0]});Q11=makeQuery(id+"F6.imprint","IMPRINT",FACE,{"disambiguationData":[TD([[makeQuery(id+"F6.imprint","IMPRINT",EDGE,{"disambiguationData":[TD([[subQ2,-1.0]])],"derivedFrom":subQ1}),-1.0]])]});}
            var Q12;
            {var subQ0=sQuery(id+"F6.wireOp",EDGE,"E7.7.9.2");var subQ1=sQuery(id+"F6.wireOp",EDGE,"E7.7.9.1");var subQ2=makeQuery(id+"F6.imprint","INTERSECT",VERTEX,{"derivedFrom":[subQ1,subQ0]});Q12=makeQuery(id+"F6.imprint","IMPRINT",FACE,{"disambiguationData":[TD([[makeQuery(id+"F6.imprint","IMPRINT",EDGE,{"disambiguationData":[TD([[subQ2,-1.0]])],"derivedFrom":subQ1}),-1.0]])]});}
            var Q13;
            {var subQ0=sQuery(id+"F6.wireOp",EDGE,"E7.6.9.2");var subQ1=sQuery(id+"F6.wireOp",EDGE,"E7.6.9.1");var subQ2=makeQuery(id+"F6.imprint","INTERSECT",VERTEX,{"derivedFrom":[subQ1,subQ0]});Q13=makeQuery(id+"F6.imprint","IMPRINT",FACE,{"disambiguationData":[TD([[makeQuery(id+"F6.imprint","IMPRINT",EDGE,{"disambiguationData":[TD([[subQ2,-1.0]])],"derivedFrom":subQ1}),-1.0]])]});}
            var Q14;
            {var subQ0=sQuery(id+"F6.wireOp",EDGE,"E7.5.9.2");var subQ1=sQuery(id+"F6.wireOp",EDGE,"E7.5.9.1");var subQ2=makeQuery(id+"F6.imprint","INTERSECT",VERTEX,{"derivedFrom":[subQ1,subQ0]});Q14=makeQuery(id+"F6.imprint","IMPRINT",FACE,{"disambiguationData":[TD([[makeQuery(id+"F6.imprint","IMPRINT",EDGE,{"disambiguationData":[TD([[subQ2,-1.0]])],"derivedFrom":subQ1}),-1.0]])]});}
            var Q15;
            {var subQ0=sQuery(id+"F6.wireOp",EDGE,"E7.0.9.1");Q15=makeQuery(id+"F6.imprint","IMPRINT",FACE,{"disambiguationData":[TD([[makeQuery(id+"F6.imprint","IMPRINT",EDGE,{"derivedFrom":subQ0}),-1.0]])]});}
            var Q16;
            {var subQ0=sQuery(id+"F6.wireOp",EDGE,"E7.1.9.2");var subQ1=sQuery(id+"F6.wireOp",EDGE,"E7.1.9.1");var subQ2=makeQuery(id+"F6.imprint","INTERSECT",VERTEX,{"derivedFrom":[subQ1,subQ0]});Q16=makeQuery(id+"F6.imprint","IMPRINT",FACE,{"disambiguationData":[TD([[makeQuery(id+"F6.imprint","IMPRINT",EDGE,{"disambiguationData":[TD([[subQ2,-1.0]])],"derivedFrom":subQ1}),-1.0]])]});}
            var Q17;
            {var subQ0=sQuery(id+"F6.wireOp",EDGE,"E7.2.9.2");var subQ1=sQuery(id+"F6.wireOp",EDGE,"E7.2.9.1");var subQ2=makeQuery(id+"F6.imprint","INTERSECT",VERTEX,{"derivedFrom":[subQ1,subQ0]});Q17=makeQuery(id+"F6.imprint","IMPRINT",FACE,{"disambiguationData":[TD([[makeQuery(id+"F6.imprint","IMPRINT",EDGE,{"disambiguationData":[TD([[subQ2,-1.0]])],"derivedFrom":subQ1}),-1.0]])]});}
            var Q18;
            {var subQ0=sQuery(id+"F6.wireOp",EDGE,"E7.3.9.2");var subQ1=sQuery(id+"F6.wireOp",EDGE,"E7.3.9.1");var subQ2=makeQuery(id+"F6.imprint","INTERSECT",VERTEX,{"derivedFrom":[subQ1,subQ0]});Q18=makeQuery(id+"F6.imprint","IMPRINT",FACE,{"disambiguationData":[TD([[makeQuery(id+"F6.imprint","IMPRINT",EDGE,{"disambiguationData":[TD([[subQ2,-1.0]])],"derivedFrom":subQ1}),-1.0]])]});}
            var Q19;
            {var subQ0=sQuery(id+"F6.wireOp",EDGE,"E7.4.9.2");var subQ1=sQuery(id+"F6.wireOp",EDGE,"E7.4.9.1");var subQ2=makeQuery(id+"F6.imprint","INTERSECT",VERTEX,{"derivedFrom":[subQ1,subQ0]});Q19=makeQuery(id+"F6.imprint","IMPRINT",FACE,{"disambiguationData":[TD([[makeQuery(id+"F6.imprint","IMPRINT",EDGE,{"disambiguationData":[TD([[subQ2,-1.0]])],"derivedFrom":subQ1}),-1.0]])]});}
            extrude(context, id + "F7", {"entities" : qUnion([Q0, Q1, Q2, Q3, Q4, Q5, Q6, Q7, Q8, Q9, Q10, Q11, Q12, Q13, Q14, Q15, Q16, Q17, Q18, Q19]), "operationType" : NewBodyOperationType.REMOVE, "endBound" : BoundingType.THROUGH_ALL, "oppositeDirection" : true, "depth" : 25 * mm});
        }
        {
            var Q0;
            {var subQ0=sQuery(id+"F0.wireOp",EDGE,"E0.right");var subQ1=sQuery(id+"F0.wireOp",EDGE,"E0.top");var subQ2=sQuery(id+"F0.wireOp",EDGE,"E0.bottom");Q0=makeQuery(id+"F3.boolean.opBoolean","SPLIT",FACE,{"disambiguationData":[TD([makeQuery(id+"F1.opExtrude","SWEPT_FACE",FACE,{"disambiguationData":[OSD([subQ0])]})])],"derivedFrom":makeQuery(id+"F1.opExtrude","CAP_FACE",FACE,{"disambiguationData":[OSD([subQ2,subQ1,sQuery(id+"F0.wireOp",EDGE,"E0.left"),subQ0])],"isStart":false})});}
            var sketch = newSketch(context, id + "F8", { "sketchPlane" : qUnion([Q0])});
            skLineSegment(sketch, "E8", {"start": v(-8, 1.5) * mm, "end": v(-7.46, -1.5) * mm});
            skSolve(sketch);
        }
        {
            var Q0;
            {var subQ0=sQuery(id+"F8.wireOp",EDGE,"E8");Q0=makeQuery(id+"F8.imprint","IMPRINT",FACE,{"disambiguationData":[TD([[makeQuery(id+"F8.imprint","IMPRINT",EDGE,{"derivedFrom":subQ0}),-1.0]])]});}
            extrude(context, id + "F9", {"entities" : qUnion([Q0]), "operationType" : NewBodyOperationType.REMOVE, "endBound" : BoundingType.THROUGH_ALL, "oppositeDirection" : true, "depth" : 25 * mm});
        }
    });
